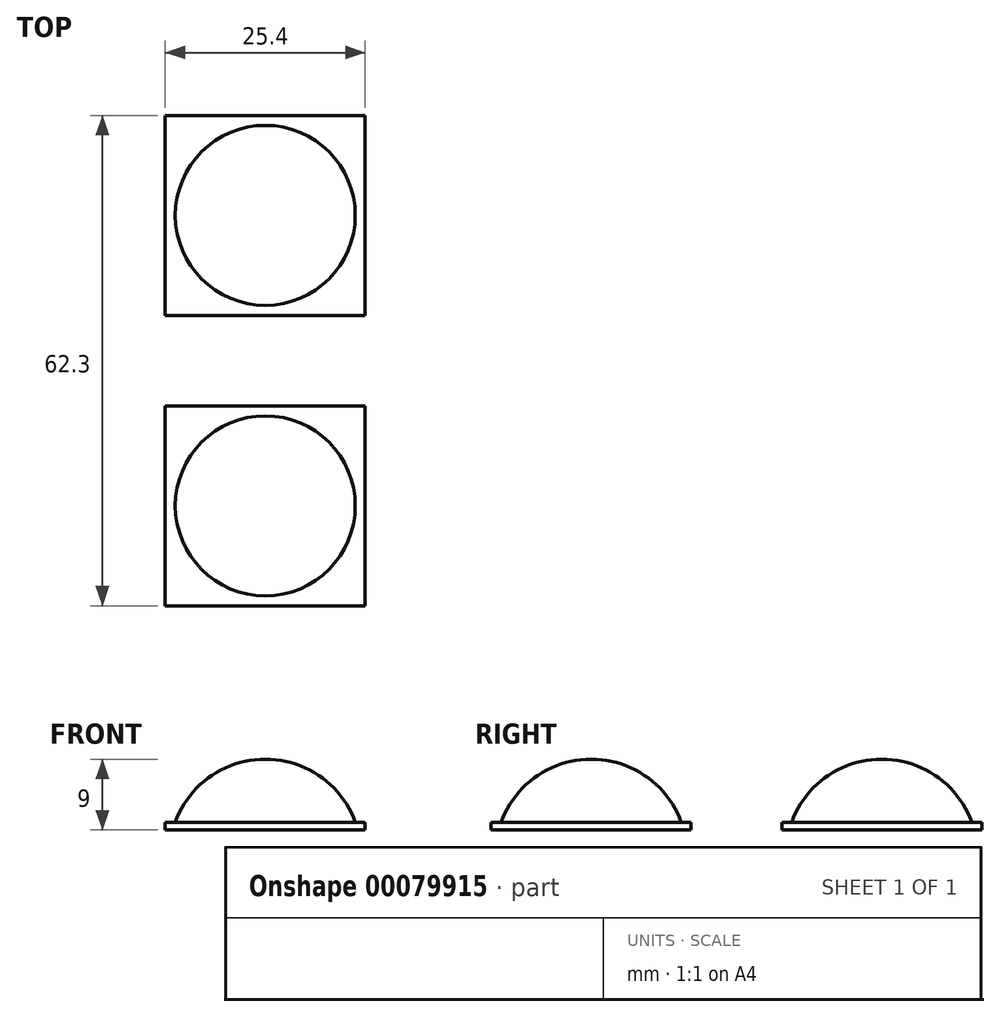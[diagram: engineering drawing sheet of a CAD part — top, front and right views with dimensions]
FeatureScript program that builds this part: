
annotation { "Feature Type Name" : "Feature", "Feature Type Description" : "" }
export const myFeature = defineFeature(function(context is Context, id is Id, definition is map)
    precondition{}
    {
        {
            var Q0;
            Q0=qCreatedBy(makeId("Top.planeOp"),FACE);
            var sketch = newSketch(context, id + "F0", { "sketchPlane" : qUnion([Q0])});
            skLineSegment(sketch, "E0.bottom", {"start": v(12.7, -12.7) * mm, "end": v(-12.7, -12.7) * mm});
            skLineSegment(sketch, "E0.top", {"start": v(12.7, 12.7) * mm, "end": v(-12.7, 12.7) * mm});
            skLineSegment(sketch, "E0.left", {"start": v(12.7, -12.7) * mm, "end": v(12.7, 12.7) * mm});
            skLineSegment(sketch, "E0.right", {"start": v(-12.7, -12.7) * mm, "end": v(-12.7, 12.7) * mm});
            skPoint(sketch, "E0.middle", {"position": v(0, 0) * mm});
            skCircle(sketch, "E1", {"center": v(0, 0) * mm, "radius": 11.43 * mm});
            skCircle(sketch, "E2", {"center": v(0, 0) * mm, "radius": 10.16 * mm});
            skSolve(sketch);
        }
        {
            var Q0;
            Q0=makeQuery(id+"F0.imprint","IMPRINT",FACE,{"disambiguationData":[TD([[makeQuery(id+"F0.imprint","IMPRINT",EDGE,{"derivedFrom":sQuery(id+"F0.wireOp",EDGE,"E0.bottom")}),-1.0]])]});
            extrude(context, id + "F1", {"entities" : qUnion([Q0]), "depth" : 1 * mm});
        }
        {
            var Q0;
            Q0=makeQuery(id+"F0.imprint","IMPRINT",FACE,{"disambiguationData":[TD([[makeQuery(id+"F0.imprint","IMPRINT",EDGE,{"derivedFrom":sQuery(id+"F0.wireOp",EDGE,"E1")}),1.0]])]});
            var Q1;
            Q1=makeQuery(id+"F0.imprint","IMPRINT",FACE,{"disambiguationData":[TD([[makeQuery(id+"F0.imprint","IMPRINT",EDGE,{"derivedFrom":sQuery(id+"F0.wireOp",EDGE,"E2")}),1.0]])]});
            extrude(context, id + "F2", {"entities" : qUnion([Q0, Q1]), "operationType" : NewBodyOperationType.ADD, "depth" : 9 * mm});
        }
        {
            var Q0;
            Q0=makeQuery(id+"F2.opExtrude","CAP_FACE",FACE,{"disambiguationData":[OSD([sQuery(id+"F0.wireOp",EDGE,"E1")])],"isStart":false});
            fillet(context, id + "F3", {"entities" : qUnion([Q0]), "radius" : 12.1 * mm, "tangentPropagation" : true, "allowEdgeOverflow" : false});
        }
        {
            var Q0;
            Q0=makeQuery(id+"F1.opExtrude","SWEPT_BODY",BODY,{"disambiguationData":[OSD([sQuery(id+"F0.wireOp",EDGE,"E0.bottom"),sQuery(id+"F0.wireOp",EDGE,"E0.top"),sQuery(id+"F0.wireOp",EDGE,"E0.left"),sQuery(id+"F0.wireOp",EDGE,"E0.right"),sQuery(id+"F0.wireOp",EDGE,"E1")])]});
            transform(context, id + "F4", {"entities" : qUnion([Q0]), "transformType" : TransformType.TRANSLATION_3D, "dx" : 0 * mm, "dy" : 36.9 * mm, "dz" : 0 * mm, "makeCopy" : true});
        }
    });
